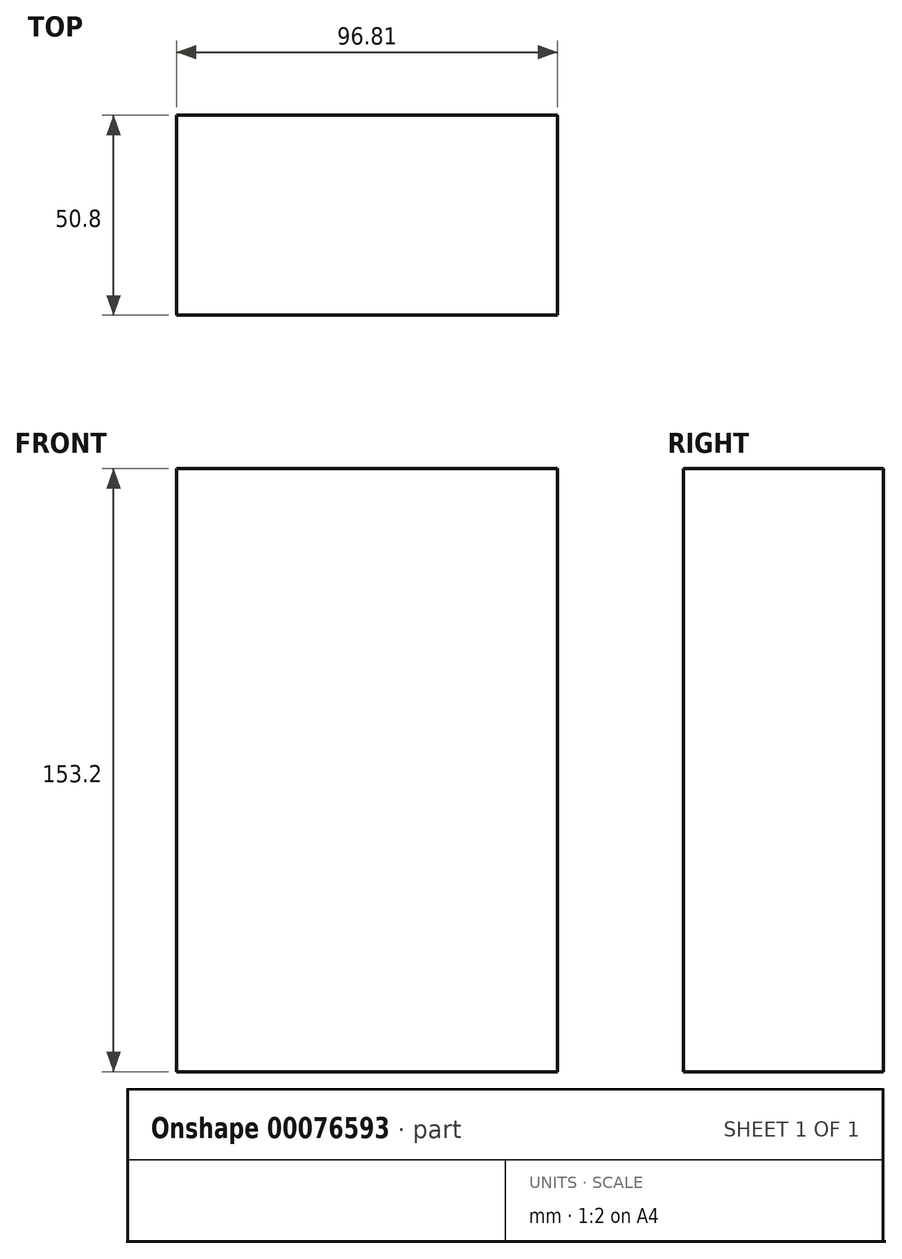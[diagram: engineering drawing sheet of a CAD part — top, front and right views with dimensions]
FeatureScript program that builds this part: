
annotation { "Feature Type Name" : "Feature", "Feature Type Description" : "" }
export const myFeature = defineFeature(function(context is Context, id is Id, definition is map)
    precondition{}
    {
        {
            var Q0;
            Q0=qCreatedBy(makeId("Front.planeOp"),FACE);
            var sketch = newSketch(context, id + "F0", { "sketchPlane" : qUnion([Q0])});
            skLineSegment(sketch, "E0.bottom", {"start": v(-76.83, 33.11) * mm, "end": v(19.98, 33.11) * mm});
            skLineSegment(sketch, "E0.top", {"start": v(-76.83, -120.1) * mm, "end": v(19.98, -120.1) * mm});
            skLineSegment(sketch, "E0.left", {"start": v(-76.83, 33.11) * mm, "end": v(-76.83, -120.1) * mm});
            skLineSegment(sketch, "E0.right", {"start": v(19.98, 33.11) * mm, "end": v(19.98, -120.1) * mm});
            skSolve(sketch);
        }
        {
            var Q0;
            Q0 = qSketchRegion(id + "F0", true);
            extrude(context, id + "F1", {"entities" : qUnion([Q0]), "depth" : 50.8 * mm});
        }
    });
